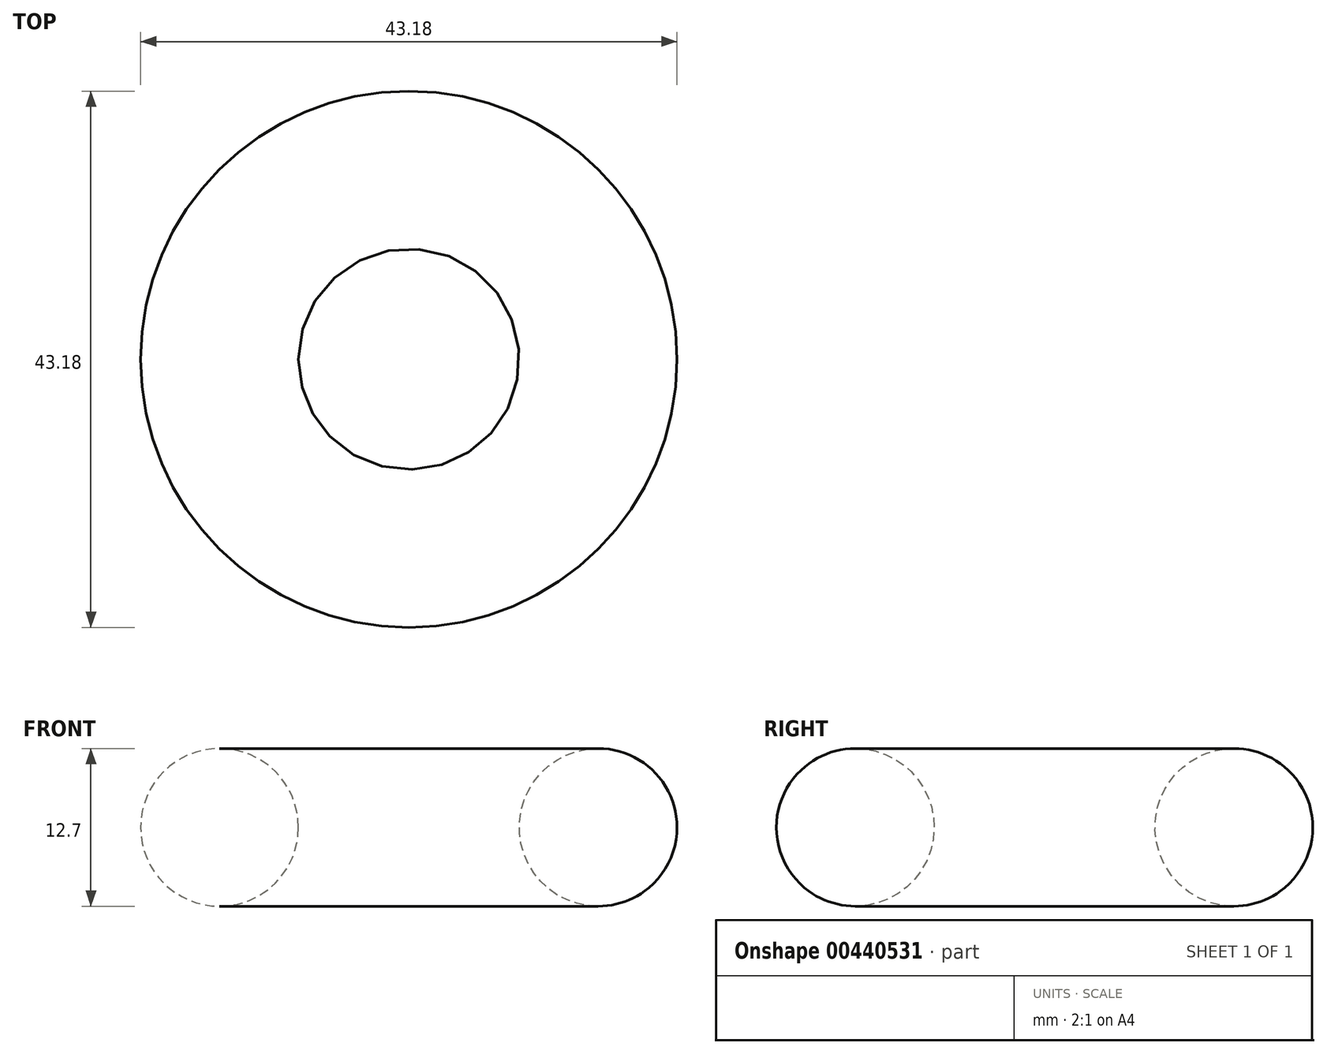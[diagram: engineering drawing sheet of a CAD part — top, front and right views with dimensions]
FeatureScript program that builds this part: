
annotation { "Feature Type Name" : "Feature", "Feature Type Description" : "" }
export const myFeature = defineFeature(function(context is Context, id is Id, definition is map)
    precondition{}
    {
        {
            var Q0;
            Q0=qCreatedBy(makeId("Front.planeOp"),FACE);
            var sketch = newSketch(context, id + "F0", { "sketchPlane" : qUnion([Q0])});
            skCircle(sketch, "E0", {"center": v(15.24, 0) * mm, "radius": 6.35 * mm});
            skLineSegment(sketch, "E1", {"start": v(0, 0) * mm, "end": v(0, 11.47) * mm, "construction": true});
            skSolve(sketch);
        }
        {
            var Q0;
            Q0 = qSketchRegion(id + "F0", true);
            var Q1;
            Q1=sQuery(id+"F0.wireOp",EDGE,"E1");
            revolve(context, id + "F1", {"entities" : qUnion([Q0]), "axis" : qUnion([Q1]), "revolveType" : RevolveType.FULL});
        }
    });
